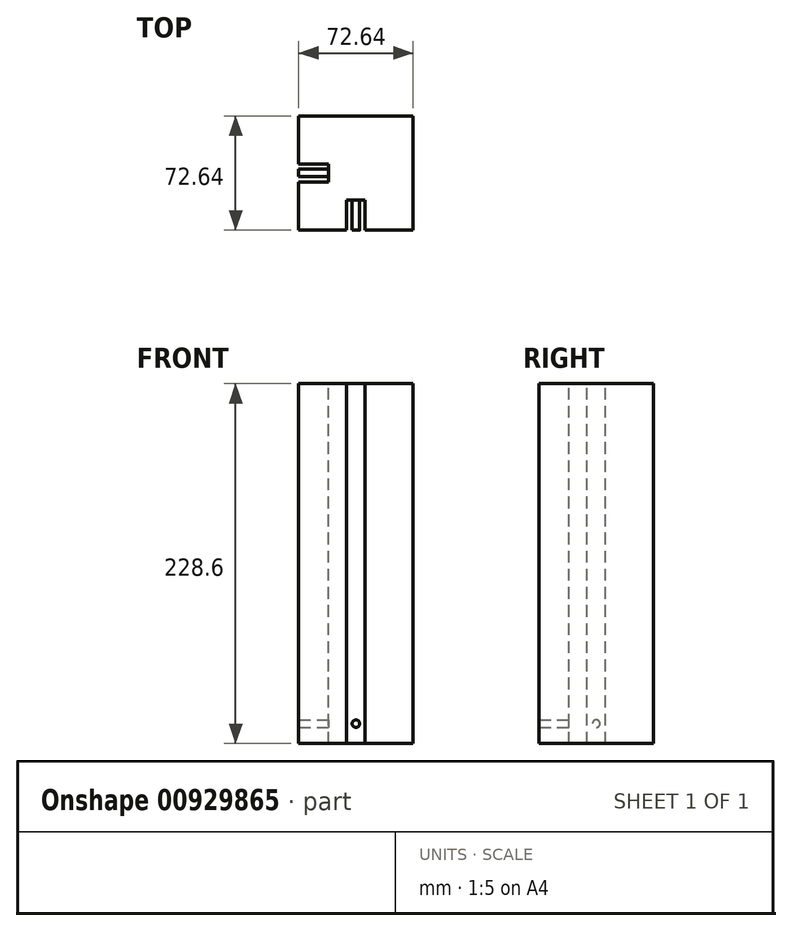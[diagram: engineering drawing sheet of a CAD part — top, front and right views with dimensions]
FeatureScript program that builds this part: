
annotation { "Feature Type Name" : "Feature", "Feature Type Description" : "" }
export const myFeature = defineFeature(function(context is Context, id is Id, definition is map)
    precondition{}
    {
        {
            var Q0;
            Q0=qCreatedBy(makeId("Top.planeOp"),FACE);
            var sketch = newSketch(context, id + "F0", { "sketchPlane" : qUnion([Q0])});
            skLineSegment(sketch, "E0.bottom", {"start": v(0, 0) * mm, "end": v(72.64, 0) * mm});
            skLineSegment(sketch, "E0.top", {"start": v(0, 72.64) * mm, "end": v(72.64, 72.64) * mm});
            skLineSegment(sketch, "E0.left", {"start": v(0, 0) * mm, "end": v(0, 72.64) * mm});
            skLineSegment(sketch, "E0.right", {"start": v(72.64, 0) * mm, "end": v(72.64, 72.64) * mm});
            skSolve(sketch);
        }
        {
            var Q0;
            Q0 = qSketchRegion(id + "F0", true);
            extrude(context, id + "F1", {"entities" : qUnion([Q0]), "depth" : 228.6 * mm, "offsetDistance" : 25.4 * mm});
        }
        {
            var Q0;
            Q0=makeQuery(id+"F1.opExtrude","CAP_FACE",FACE,{"disambiguationData":[OSD([sQuery(id+"F0.wireOp",EDGE,"E0.bottom"),sQuery(id+"F0.wireOp",EDGE,"E0.top"),sQuery(id+"F0.wireOp",EDGE,"E0.left"),sQuery(id+"F0.wireOp",EDGE,"E0.right")])],"isStart":false});
            var sketch = newSketch(context, id + "F2", { "sketchPlane" : qUnion([Q0])});
            skLineSegment(sketch, "E1.bottom", {"start": v(0, 42.16) * mm, "end": v(19.05, 42.16) * mm});
            skLineSegment(sketch, "E1.top", {"start": v(0, 30.48) * mm, "end": v(19.05, 30.48) * mm});
            skLineSegment(sketch, "E1.left", {"start": v(0, 42.16) * mm, "end": v(0, 30.48) * mm});
            skLineSegment(sketch, "E1.right", {"start": v(19.05, 42.16) * mm, "end": v(19.05, 30.48) * mm});
            skLineSegment(sketch, "E2.bottom", {"start": v(30.48, 0) * mm, "end": v(42.16, 0) * mm});
            skLineSegment(sketch, "E2.top", {"start": v(30.48, 19.05) * mm, "end": v(42.16, 19.05) * mm});
            skLineSegment(sketch, "E2.left", {"start": v(30.48, 0) * mm, "end": v(30.48, 19.05) * mm});
            skLineSegment(sketch, "E2.right", {"start": v(42.16, 0) * mm, "end": v(42.16, 19.05) * mm});
            skSolve(sketch);
        }
        {
            var Q0;
            Q0 = qSketchRegion(id + "F2", true);
            extrude(context, id + "F3", {"entities" : qUnion([Q0]), "operationType" : NewBodyOperationType.REMOVE, "endBound" : BoundingType.THROUGH_ALL, "oppositeDirection" : true, "depth" : 25.4 * mm, "offsetDistance" : 25.4 * mm});
        }
        {
            var Q0;
            Q0=makeQuery(id+"F3.boolean.opBoolean","COPY",FACE,{"derivedFrom":makeQuery(id+"F3.opExtrude","SWEPT_FACE",FACE,{"disambiguationData":[OSD([sQuery(id+"F2.wireOp",EDGE,"E2.top")])]})});
            var sketch = newSketch(context, id + "F4", { "sketchPlane" : qUnion([Q0])});
            skCircle(sketch, "E3", {"center": v(36.32, 12.7) * mm, "radius": 2.38 * mm});
            skSolve(sketch);
        }
        {
            var Q0;
            Q0 = qSketchRegion(id + "F4", true);
            var Q1;
            {var subQ0=sQuery(id+"F0.wireOp",EDGE,"E0.right");var subQ3=sQuery(id+"F0.wireOp",EDGE,"E0.bottom");Q1=makeQuery(id+"F3.boolean.opBoolean","SPLIT",FACE,{"disambiguationData":[TD([makeQuery(id+"F1.opExtrude","SWEPT_FACE",FACE,{"disambiguationData":[OSD([subQ0])]})])],"derivedFrom":makeQuery(id+"F1.opExtrude","SWEPT_FACE",FACE,{"disambiguationData":[OSD([subQ3])]})});}
            extrude(context, id + "F5", {"entities" : qUnion([Q0]), "operationType" : NewBodyOperationType.ADD, "endBound" : BoundingType.UP_TO_SURFACE, "depth" : 25.4 * mm, "endBoundEntityFace" : qUnion([Q1]), "offsetDistance" : 25.4 * mm});
        }
        {
            var Q0;
            Q0=makeQuery(id+"F3.boolean.opBoolean","COPY",FACE,{"derivedFrom":makeQuery(id+"F3.opExtrude","SWEPT_FACE",FACE,{"disambiguationData":[OSD([sQuery(id+"F2.wireOp",EDGE,"E1.right")])]})});
            var sketch = newSketch(context, id + "F6", { "sketchPlane" : qUnion([Q0])});
            skCircle(sketch, "E4", {"center": v(-36.32, 12.7) * mm, "radius": 2.38 * mm});
            skSolve(sketch);
        }
        {
            var Q0;
            Q0 = qSketchRegion(id + "F6", true);
            var Q1;
            {var subQ0=sQuery(id+"F0.wireOp",EDGE,"E0.bottom");var subQ2=sQuery(id+"F0.wireOp",EDGE,"E0.left");Q1=makeQuery(id+"F3.boolean.opBoolean","SPLIT",FACE,{"disambiguationData":[TD([makeQuery(id+"F1.opExtrude","SWEPT_FACE",FACE,{"disambiguationData":[OSD([subQ0])]})])],"derivedFrom":makeQuery(id+"F1.opExtrude","SWEPT_FACE",FACE,{"disambiguationData":[OSD([subQ2])]})});}
            extrude(context, id + "F7", {"entities" : qUnion([Q0]), "operationType" : NewBodyOperationType.ADD, "endBound" : BoundingType.UP_TO_SURFACE, "depth" : 25.4 * mm, "endBoundEntityFace" : qUnion([Q1]), "offsetDistance" : 25.4 * mm});
        }
    });
